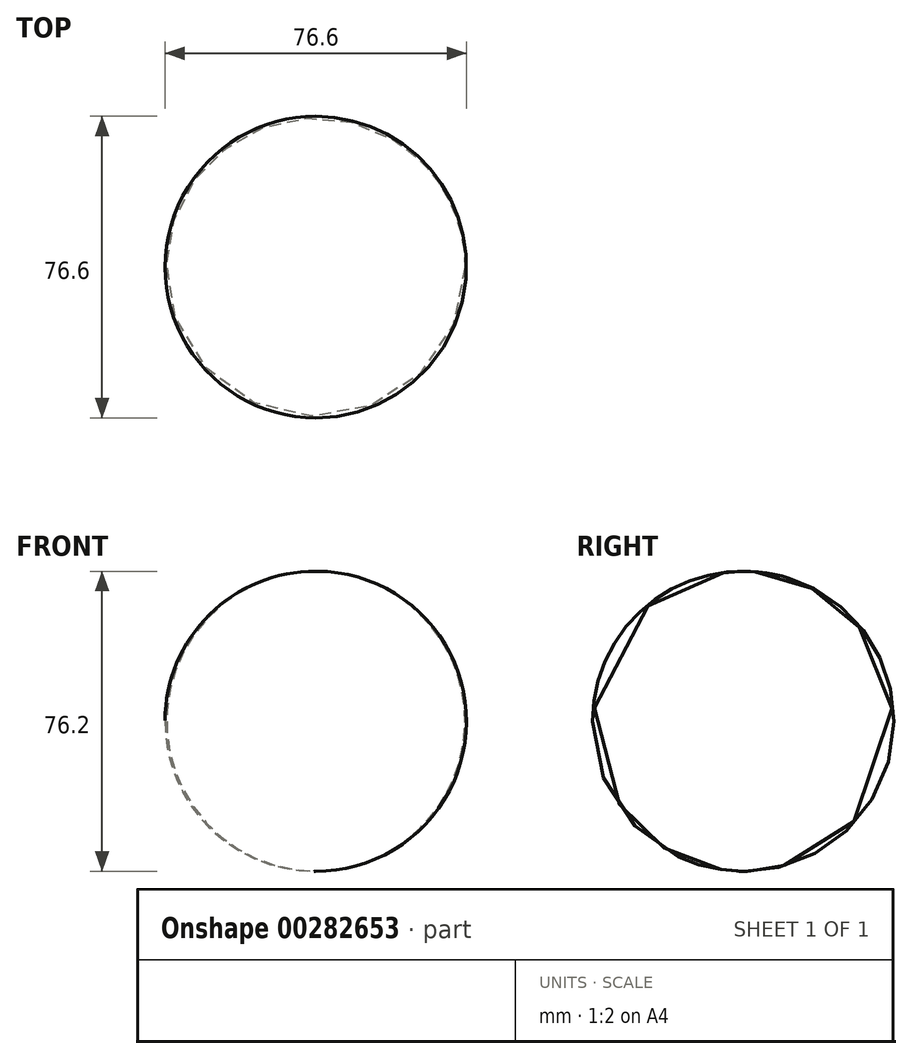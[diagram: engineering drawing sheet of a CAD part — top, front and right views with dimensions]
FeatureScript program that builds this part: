
annotation { "Feature Type Name" : "Feature", "Feature Type Description" : "" }
export const myFeature = defineFeature(function(context is Context, id is Id, definition is map)
    precondition{}
    {
        {
            var Q0;
            Q0=qCreatedBy(makeId("Front.planeOp"),FACE);
            var sketch = newSketch(context, id + "F0", { "sketchPlane" : qUnion([Q0])});
            skArc(sketch, "E0", {"start": v(0.01, 38.1) * mm, "mid": v(-38.1, 0.21) * mm, "end": v(-0.41, -38.1) * mm});
            skLineSegment(sketch, "E1", {"start": v(-0.41, -38.1) * mm, "end": v(0.01, 38.1) * mm});
            skSolve(sketch);
        }
        {
            var Q0;
            Q0=makeQuery(id+"F0.imprint","IMPRINT",FACE,{"disambiguationData":[TD([[makeQuery(id+"F0.imprint","IMPRINT",EDGE,{"derivedFrom":sQuery(id+"F0.wireOp",EDGE,"E0")}),1.0]])]});
            var Q1;
            Q1=sQuery(id+"F0.wireOp",EDGE,"E1");
            revolve(context, id + "F1", {"entities" : qUnion([Q0]), "axis" : qUnion([Q1]), "revolveType" : RevolveType.FULL});
        }
    });
